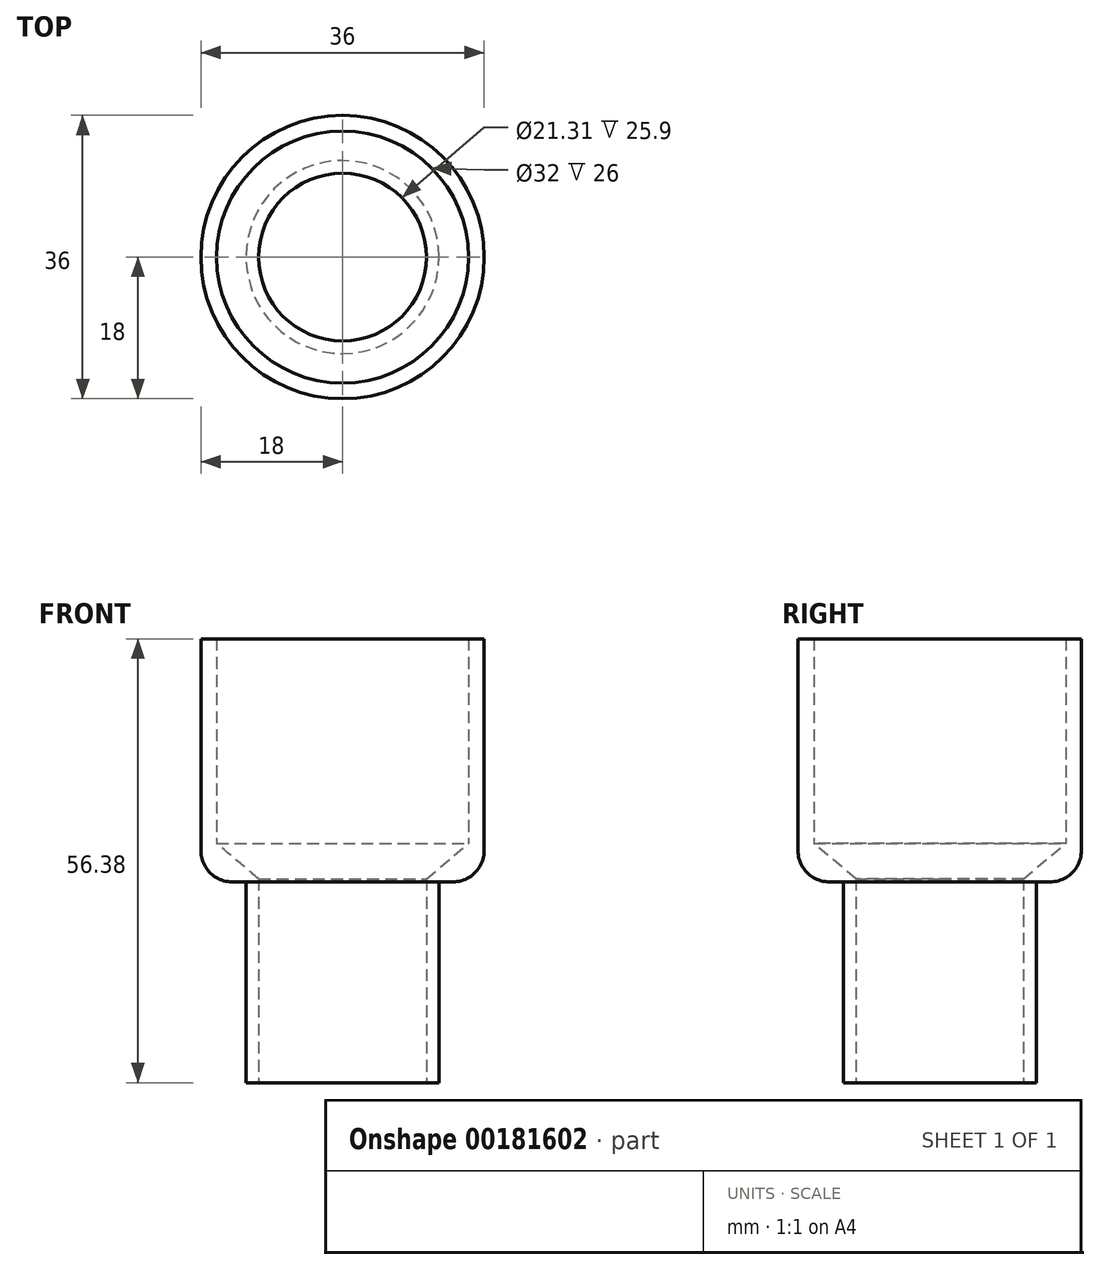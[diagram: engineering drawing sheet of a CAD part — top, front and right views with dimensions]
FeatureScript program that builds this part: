
annotation { "Feature Type Name" : "Feature", "Feature Type Description" : "" }
export const myFeature = defineFeature(function(context is Context, id is Id, definition is map)
    precondition{}
    {
        {
            var Q0;
            Q0=qCreatedBy(makeId("Front.planeOp"),FACE);
            var sketch = newSketch(context, id + "F0", { "sketchPlane" : qUnion([Q0])});
            skLineSegment(sketch, "E0", {"start": v(0, 0) * mm, "end": v(0, 56.38) * mm, "construction": true});
            skLineSegment(sketch, "E1", {"start": v(10.66, 0) * mm, "end": v(10.66, 25.9) * mm});
            skLineSegment(sketch, "E2", {"start": v(10.66, 25.9) * mm, "end": v(16, 30.38) * mm});
            skLineSegment(sketch, "E3", {"start": v(16, 30.38) * mm, "end": v(16, 56.38) * mm});
            skLineSegment(sketch, "E4", {"start": v(16, 56.38) * mm, "end": v(18, 56.38) * mm});
            skLineSegment(sketch, "E5", {"start": v(18, 56.38) * mm, "end": v(18, 25.5) * mm});
            skLineSegment(sketch, "E6", {"start": v(18, 25.5) * mm, "end": v(12.26, 25.5) * mm});
            skLineSegment(sketch, "E7", {"start": v(12.26, 25.5) * mm, "end": v(12.26, 0) * mm});
            skLineSegment(sketch, "E8", {"start": v(12.26, 0) * mm, "end": v(10.66, 0) * mm});
            skSolve(sketch);
        }
        {
            var Q0;
            Q0 = qSketchRegion(id + "F0", true);
            var Q1;
            Q1=sQuery(id+"F0.wireOp",EDGE,"E0");
            revolve(context, id + "F1", {"surfaceOperationType" : NewSurfaceOperationType.NEW, "entities" : qUnion([Q0]), "axis" : qUnion([Q1]), "revolveType" : RevolveType.FULL});
        }
        {
            var Q0;
            Q0=makeQuery(id+"F1.opRevolve","SWEPT_EDGE",EDGE,{"disambiguationData":[OSD([sQuery(id+"F0.wireOp",EDGE,"E5"),sQuery(id+"F0.wireOp",EDGE,"E6")])]});
            fillet(context, id + "F2", {"entities" : qUnion([Q0]), "tangentPropagation" : true, "radius" : 4 * mm, "defaultsChanged" : true, "vertexSettings" : [], "allowEdgeOverflow" : false});
        }
    });
